# Revit family: VF3_DN15-DN100_AMV(E) 55(56)_RFA_1
name_source: partatom
category: Pipe Accessories
units: mm (PartAtom-declared; Revit-internal decimal feet)

## family parameters
Always vertical = Yes
Cut with Voids When Loaded = No
OmniClass Number = 23.65.55.14.17
OmniClass Title = Adjusting/Controlling Valves for Liquid Services
Part Type = Valve - Breaks Into
Round Connector Dimension = Use Diameter
Shared = No
Work Plane-Based = No

## types (13) — shared parameters
082H3020 = AMV(E) 55(56)_RFA : AMV 55_24V_082H3020
082H3021 = AMV(E) 55(56)_RFA : AMV 55_230V_082H3021
082H3023 = AMV(E) 55(56)_RFA : AMV 56_24V_082H3023
082H3024 = AMV(E) 55(56)_RFA : AMV 56_230V_082H3024
082H3025 = AMV(E) 55(56)_RFA : AME 56_082H3025
Actuator Type = AMV(E) 55(56)_RFA : AME 55_082H3022
Adapter Type = Adapter_AMV(E)_RFA : Adapter_AMV(E) 55(56)_DN65-80_065Z0312
C1 = 8 mm  [stored 0.0262467 ft]
Connection = Flange
Description = Motorized Control Valve
H2 = 95 mm
HB2 = 9 mm  [stored 0.0295276 ft]
HB2__ve = -9 mm
HD = 14 mm  [stored 0.0459318 ft]
HT1 = 43 mm
HT2 = 24 mm
IfcExportAs = IfcValveType
IfcExportType = VF3
K = 65 mm
L2D = 130 mm
L2D_Min = 30 mm
LM = 110 mm
LM1 = 55 mm
LOD 200 = No
LOD 350 = Yes
Manufacturer = Danfoss
Max Medium Temperature = 130 °C
Min Medium Temperature = -10 °C
N = 4
N1 = 13 mm
Nominal Pressure = PN 16
Power = 9 VA
R = 8 mm  [stored 0.0262467 ft]
R4 = 3 mm  [stored 0.00984252 ft]
URL = https://store.danfoss.com
V_SMALL LOD 200 = No
Valve Body Material = Danfoss Grey Iron
Voltage = 24 V
Y1 = 15 mm  [stored 0.0492126 ft]
Z = 22 mm
zero-valued in all types: CAT

## per-type parameters (varying)
- VF3_DN20_Kv6.3_065Z0256: A1=3 mm  [stored 0.00984252 ft]; A1_Flow Pipe=168.00°; A2=47.12°; A3=15.00°; A_Flow Pipe=165.00°; Adapter assembly=2 mm  [stored 0.00656168 ft]; C=3 mm  [stored 0.00984252 ft]; C2_ve=-14 mm; C__ve=-3 mm  [stored -0.00984252 ft]; D=20 mm; DN=20 mm; DN65 to DN100=No; DN65 to DN80=No; D_Connection End=60 mm; D_Flange=105 mm; Depth_Flange=14 mm  [stored 0.0459318 ft]; EXT2=-54 mm  [stored -0.177165 ft]; EXT3=18 mm  [stored 0.0590551 ft]; Extrusion Bottom=55 mm; Extrusion Top=27 mm; Extrusion Top 2=8 mm  [stored 0.0262467 ft]; Flange Bottom Depth=14 mm  [stored 0.0459318 ft]; H1=34 mm; HB1=40 mm; HB1__ve=-40 mm  [stored -0.131234 ft]; HB3=3 mm  [stored 0.00984252 ft]; HE=0 mm  [stored 0 ft]; HE1=57 mm; HH1=87 mm; HH2=70 mm; HR=28 mm; HR1=25 mm; Kvs=6.3 m³/h; L=150 mm; L2=75 mm; L_EXT=85 mm; L_S=48 mm; M=3 mm  [stored 0.00984252 ft]; Model=065Z0256; Model Type=VF3_DN20_Kv6.3; N2=5 mm  [stored 0.0164042 ft]; Offset Flow Pipe_1=6 mm  [stored 0.019685 ft]; Offset Flow Pipe_2=6 mm  [stored 0.019685 ft]; R1=23 mm; R1_1=20 mm; R1_1_1=20 mm; R1_2=13 mm; R1_Revolve=10 mm  [stored 0.0328084 ft]; R2=11 mm  [stored 0.0360892 ft]; R2_Revolve=8 mm  [stored 0.0262467 ft]; R6=29 mm; R6_2=31 mm; R_Flange Bottom=53 mm; R_Flow Pipe=17 mm; R_Top=13 mm; R_Vertical Valve=18 mm  [stored 0.0590551 ft]; R_arc=35 mm; Stroke=10 mm; TH1=97 mm; TL=150 mm; V_DN100=No; V_SMALL=Yes; W=105 mm; W1=18 mm  [stored 0.0590551 ft]; W2=20 mm; W2D=14 mm  [stored 0.0459318 ft]; Weight=3.55 kg; l_Top=3 mm  [stored 0.00984252 ft]
- VF3_DN25_Kv10_065Z0257: A1=5 mm  [stored 0.0164042 ft]; A1_Flow Pipe=166.00°; A2=47.12°; A3=10.00°; A_Flow Pipe=165.00°; Adapter assembly=2 mm  [stored 0.00656168 ft]; C=3 mm  [stored 0.00984252 ft]; C2_ve=-14 mm; C__ve=-3 mm  [stored -0.00984252 ft]; D=25 mm; DN=25 mm; DN65 to DN100=No; DN65 to DN80=No; D_Connection End=70 mm; D_Flange=115 mm; Depth_Flange=14 mm  [stored 0.0459318 ft]; EXT2=-58 mm  [stored -0.190289 ft]; EXT3=15 mm  [stored 0.0492126 ft]; Extrusion Bottom=62 mm; Extrusion Top=25 mm; Extrusion Top 2=5 mm  [stored 0.0164042 ft]; Flange Bottom Depth=15 mm  [stored 0.0492126 ft]; H1=37 mm; HB1=40 mm; HB1__ve=-40 mm  [stored -0.131234 ft]; HB3=3 mm  [stored 0.00984252 ft]; HE=0 mm  [stored 0 ft]; HE1=60 mm; HH1=91 mm; HH2=75 mm; HR=31 mm; HR1=25 mm; Kvs=10.0 m³/h; L=160 mm; L2=80 mm; L_EXT=90 mm; L_S=48 mm; M=3 mm  [stored 0.00984252 ft]; Model=065Z0257; Model Type=VF3_DN25_Kv10; N2=5 mm  [stored 0.0164042 ft]; Offset Flow Pipe_1=9 mm  [stored 0.0295276 ft]; Offset Flow Pipe_2=6 mm  [stored 0.019685 ft]; R1=25 mm; R1_1=21 mm; R1_1_1=21 mm; R1_2=13 mm; R1_Revolve=12 mm  [stored 0.0393701 ft]; R2=11 mm  [stored 0.0360892 ft]; R2_Revolve=9 mm  [stored 0.0295276 ft]; R6=34 mm; R6_2=36 mm; R_Flange Bottom=58 mm; R_Flow Pipe=19 mm  [stored 0.062336 ft]; R_Top=13 mm; R_Vertical Valve=20 mm; R_arc=36 mm; Stroke=10 mm; TH1=101 mm; TL=160 mm; V_DN100=No; V_SMALL=Yes; W=115 mm; W1=18 mm  [stored 0.0590551 ft]; W2=20 mm; W2D=15 mm  [stored 0.0492126 ft]; Weight=4.54 kg; l_Top=3 mm  [stored 0.00984252 ft]
- VF3_DN32_Kv16_065Z0258: A1=3 mm  [stored 0.00984252 ft]; A1_Flow Pipe=170.00°; A2=47.12°; A3=16.00°; A_Flow Pipe=168.00°; Adapter assembly=1 mm  [stored 0.00328084 ft]; C=3 mm  [stored 0.00984252 ft]; C2_ve=-16 mm  [stored -0.0524934 ft]; C__ve=-3 mm  [stored -0.00984252 ft]; D=32 mm; DN=32 mm; DN65 to DN100=No; DN65 to DN80=No; D_Connection End=80 mm; D_Flange=140 mm; Depth_Flange=16 mm  [stored 0.0524934 ft]; EXT2=-62 mm; EXT3=20 mm; Extrusion Bottom=73 mm; Extrusion Top=35 mm; Extrusion Top 2=10 mm  [stored 0.0328084 ft]; Flange Bottom Depth=16 mm  [stored 0.0524934 ft]; H1=42 mm; HB1=40 mm; HB1__ve=-40 mm  [stored -0.131234 ft]; HB3=3 mm  [stored 0.00984252 ft]; HE=0 mm  [stored 0 ft]; HE1=65 mm; HH1=96 mm; HH2=80 mm; HR=31 mm; HR1=33 mm; Kvs=16.0 m³/h; L=180 mm; L2=90 mm; L_EXT=100 mm; L_S=48 mm; M=3 mm  [stored 0.00984252 ft]; Model=065Z0258; Model Type=VF3_DN32_Kv16; N2=5 mm  [stored 0.0164042 ft]; Offset Flow Pipe_1=7 mm  [stored 0.0229659 ft]; Offset Flow Pipe_2=9 mm  [stored 0.0295276 ft]; R1=29 mm; R1_1=24 mm; R1_1_1=24 mm; R1_2=24 mm; R1_Revolve=17 mm; R2=13 mm; R2_Revolve=14 mm  [stored 0.0459318 ft]; R6=39 mm; R6_2=42 mm; R_Flange Bottom=70 mm; R_Flow Pipe=24 mm; R_Top=13 mm; R_Vertical Valve=25 mm; R_arc=41 mm; Stroke=15 mm; TH1=106 mm; TL=180 mm; V_DN100=No; V_SMALL=Yes; W=140 mm; W1=22 mm; W2=26 mm; W2D=15 mm  [stored 0.0492126 ft]; Weight=6.90 kg; l_Top=3 mm  [stored 0.00984252 ft]
- VF3_DN40_Kv25_065Z0259: A1=3 mm  [stored 0.00984252 ft]; A1_Flow Pipe=165.00°; A2=47.12°; A3=15.00°; A_Flow Pipe=166.00°; Adapter assembly=1 mm  [stored 0.00328084 ft]; C=3 mm  [stored 0.00984252 ft]; C2_ve=-16 mm  [stored -0.0524934 ft]; C__ve=-3 mm  [stored -0.00984252 ft]; D=40 mm; DN=40 mm; DN65 to DN100=No; DN65 to DN80=No; D_Connection End=90 mm; D_Flange=150 mm; Depth_Flange=16 mm  [stored 0.0524934 ft]; EXT2=-72 mm; EXT3=30 mm; Extrusion Bottom=74 mm; Extrusion Top=37 mm; Extrusion Top 2=10 mm  [stored 0.0328084 ft]; Flange Bottom Depth=16 mm  [stored 0.0524934 ft]; H1=65 mm; HB1=40 mm; HB1__ve=-40 mm  [stored -0.131234 ft]; HB3=3 mm  [stored 0.00984252 ft]; HE=6 mm  [stored 0.019685 ft]; HE1=94 mm; HH1=124 mm; HH2=90 mm; HR=40 mm; HR1=42 mm; Kvs=25.0 m³/h; L=200 mm; L2=100 mm; L_EXT=120 mm; L_S=48 mm; M=3 mm  [stored 0.00984252 ft]; Model=065Z0259; Model Type=VF3_DN40_Kv25; N2=12 mm  [stored 0.0393701 ft]; Offset Flow Pipe_1=10 mm  [stored 0.0328084 ft]; Offset Flow Pipe_2=10 mm  [stored 0.0328084 ft]; R1=36 mm; R1_1=29 mm; R1_1_1=29 mm; R1_2=18 mm  [stored 0.0590551 ft]; R1_Revolve=25 mm; R2=11 mm  [stored 0.0360892 ft]; R2_Revolve=23 mm; R6=44 mm; R6_2=47 mm; R_Flange Bottom=75 mm; R_Flow Pipe=28 mm; R_Top=13 mm; R_Vertical Valve=29 mm; R_arc=50 mm; Stroke=15 mm; TH1=134 mm; TL=200 mm; V_DN100=No; V_SMALL=Yes; W=150 mm; W1=23 mm; W2=31 mm; W2D=15 mm  [stored 0.0492126 ft]; Weight=9.05 kg; l_Top=3 mm  [stored 0.00984252 ft]
- VF3_DN50_Kv40_065Z0260: A1=1 mm  [stored 0.00328084 ft]; A1_Flow Pipe=165.00°; A2=47.12°; A3=20.00°; A_Flow Pipe=168.00°; Adapter assembly=1 mm  [stored 0.00328084 ft]; C=4 mm  [stored 0.0131234 ft]; C2_ve=-16 mm  [stored -0.0524934 ft]; C__ve=-4 mm  [stored -0.0131234 ft]; D=50 mm; DN=50 mm; DN65 to DN100=No; DN65 to DN80=No; D_Connection End=105 mm; D_Flange=165 mm; Depth_Flange=16 mm  [stored 0.0524934 ft]; EXT2=-80 mm  [stored -0.262467 ft]; EXT3=30 mm; Extrusion Bottom=83 mm; Extrusion Top=50 mm; Extrusion Top 2=10 mm  [stored 0.0328084 ft]; Flange Bottom Depth=16 mm  [stored 0.0524934 ft]; H1=77 mm; HB1=40 mm; HB1__ve=-40 mm  [stored -0.131234 ft]; HB3=4 mm  [stored 0.0131234 ft]; HE=6 mm  [stored 0.019685 ft]; HE1=106 mm; HH1=137 mm; HH2=100 mm; HR=46 mm; HR1=55 mm; Kvs=40.0 m³/h; L=230 mm; L2=115 mm; L_EXT=150 mm; L_S=65 mm; M=3 mm  [stored 0.00984252 ft]; Model=065Z0260; Model Type=VF3_DN50_Kv40; N2=21 mm; Offset Flow Pipe_1=8 mm  [stored 0.0262467 ft]; Offset Flow Pipe_2=15 mm  [stored 0.0492126 ft]; R1=44 mm; R1_1=35 mm; R1_1_1=35 mm; R1_2=21 mm; R1_Revolve=33 mm; R2=11 mm  [stored 0.0360892 ft]; R2_Revolve=28 mm; R6=51 mm; R6_2=54 mm; R_Flange Bottom=83 mm; R_Flow Pipe=30 mm; R_Top=13 mm; R_Vertical Valve=37 mm; R_arc=59 mm; Stroke=15 mm; TH1=147 mm; TL=230 mm; V_DN100=No; V_SMALL=Yes; W=165 mm; W1=32 mm; W2=34 mm; W2D=15 mm  [stored 0.0492126 ft]; Weight=12.79 kg; l_Top=3 mm  [stored 0.00984252 ft]
- VF3_DN65_Kv63_065Z0261: A1=70 mm; A1_Flow Pipe=165.00°; A2=30.00°; A3=20.00°; A_Flow Pipe=165.00°; Adapter assembly=5 mm  [stored 0.0164042 ft]; C=4 mm  [stored 0.0131234 ft]; C2_ve=-18 mm  [stored -0.0590551 ft]; C__ve=-4 mm  [stored -0.0131234 ft]; D=65 mm; DN=65 mm; DN65 to DN100=Yes; DN65 to DN80=Yes; D_Connection End=105 mm; D_Flange=185 mm; Depth_Flange=18 mm  [stored 0.0590551 ft]; EXT2=-97 mm  [stored -0.318241 ft]; EXT3=41 mm; Extrusion Bottom=100 mm; Extrusion Top=65 mm; Extrusion Top 2=20 mm; Flange Bottom Depth=20 mm; H1=84 mm; HB1=45 mm; HB1__ve=-45 mm  [stored -0.147638 ft]; HB3=5 mm  [stored 0.0164042 ft]; HE=7 mm  [stored 0.0229659 ft]; HE1=112 mm; HH1=148 mm; HH2=120 mm; HR=58 mm; HR1=70 mm; Kvs=63.0 m³/h; L=290 mm; L2=145 mm; L_EXT=185 mm; L_S=97 mm; M=3 mm  [stored 0.00984252 ft]; Model=065Z0261; Model Type=VF3_DN65_Kv63; N2=27 mm; Offset Flow Pipe_1=16 mm  [stored 0.0524934 ft]; Offset Flow Pipe_2=25 mm; R1=55 mm; R1_1=50 mm; R1_1_1=50 mm; R1_2=27 mm; R1_Revolve=48 mm; R2=11 mm  [stored 0.0360892 ft]; R2_Revolve=39 mm; R6=61 mm; R6_2=66 mm; R_Flange Bottom=93 mm; R_Flow Pipe=41 mm; R_Top=13 mm; R_Vertical Valve=45 mm; R_arc=76 mm; Stroke=20 mm; TH1=158 mm; TL=290 mm; V_DN100=No; V_SMALL=Yes; W=185 mm; W1=35 mm; W2=48 mm; W2D=15 mm  [stored 0.0492126 ft]; Weight=19.18 kg; l_Top=3 mm  [stored 0.00984252 ft]
- VF3_DN80_Kv100_065Z0262: A1=95 mm; A1_Flow Pipe=165.00°; A2=41.00°; A3=25.00°; A_Flow Pipe=169.00°; Adapter assembly=5 mm  [stored 0.0164042 ft]; C=6 mm  [stored 0.019685 ft]; C2_ve=-19 mm  [stored -0.062336 ft]; C__ve=-6 mm; D=80 mm; DN=80 mm; DN65 to DN100=Yes; DN65 to DN80=Yes; D_Connection End=130 mm; D_Flange=200 mm; Depth_Flange=19 mm  [stored 0.062336 ft]; EXT2=-130 mm  [stored -0.426509 ft]; EXT3=50 mm; Extrusion Bottom=132 mm; Extrusion Top=83 mm; Extrusion Top 2=20 mm; Flange Bottom Depth=20 mm; H1=100 mm; HB1=50 mm; HB1__ve=-50 mm  [stored -0.164042 ft]; HB3=4 mm  [stored 0.0131234 ft]; HE=7 mm  [stored 0.0229659 ft]; HE1=128 mm; HH1=164 mm; HH2=155 mm; HR=68 mm; HR1=70 mm; Kvs=100.0 m³/h; L=316 mm; L2=158 mm; L_EXT=200 mm; L_S=95 mm; M=3 mm  [stored 0.00984252 ft]; Model=065Z0262; Model Type=VF3_DN80_Kv100; N2=25 mm; Offset Flow Pipe_1=25 mm; Offset Flow Pipe_2=21 mm; R1=63 mm; R1_1=56 mm; R1_1_1=55 mm; R1_2=27 mm; R1_Revolve=63 mm; R2=100 mm; R2_Revolve=50 mm; R6=64 mm; R6_2=69 mm; R_Flange Bottom=100 mm; R_Flow Pipe=44 mm; R_Top=13 mm; R_Vertical Valve=55 mm; R_arc=94 mm; Stroke=20 mm; TH1=174 mm; TL=316 mm; V_DN100=No; V_SMALL=Yes; W=200 mm; W1=40 mm; W2=55 mm; W2D=15 mm  [stored 0.0492126 ft]; Weight=23.73 kg; l_Top=3 mm  [stored 0.00984252 ft]
- VF3_DN15_Kv2.5_065Z0254: A1=3 mm  [stored 0.00984252 ft]; A1_Flow Pipe=168.00°; A2=47.12°; A3=13.00°; A_Flow Pipe=166.00°; Adapter assembly=2 mm  [stored 0.00656168 ft]; C=3 mm  [stored 0.00984252 ft]; C2_ve=-12 mm  [stored -0.0393701 ft]; C__ve=-3 mm  [stored -0.00984252 ft]; D=15 mm  [stored 0.0492126 ft]; DN=15 mm; DN65 to DN100=No; DN65 to DN80=No; D_Connection End=50 mm; D_Flange=95 mm; Depth_Flange=12 mm  [stored 0.0393701 ft]; EXT2=-50 mm  [stored -0.164042 ft]; EXT3=20 mm; Extrusion Bottom=49 mm; Extrusion Top=21 mm; Extrusion Top 2=5 mm  [stored 0.0164042 ft]; Flange Bottom Depth=12 mm  [stored 0.0393701 ft]; H1=31 mm; HB1=40 mm; HB1__ve=-40 mm  [stored -0.131234 ft]; HB3=3 mm  [stored 0.00984252 ft]; HE=0 mm  [stored 0 ft]; HE1=54 mm; HH1=85 mm; HH2=63 mm; HR=27 mm; HR1=23 mm; Kvs=2.5 m³/h; L=130 mm; L2=65 mm; L_EXT=80 mm; L_S=48 mm; M=2 mm  [stored 0.00656168 ft]; Model=065Z0254; Model Type=VF3_DN15_Kv2.5; N2=5 mm  [stored 0.0164042 ft]; Offset Flow Pipe_1=7 mm  [stored 0.0229659 ft]; Offset Flow Pipe_2=6 mm  [stored 0.019685 ft]; R1=21 mm; R1_1=16 mm  [stored 0.0524934 ft]; R1_1_1=16 mm  [stored 0.0524934 ft]; R1_2=13 mm; R1_Revolve=9 mm  [stored 0.0295276 ft]; R2=11 mm  [stored 0.0360892 ft]; R2_Revolve=6 mm  [stored 0.019685 ft]; R6=23 mm; R6_2=26 mm; R_Flange Bottom=48 mm; R_Flow Pipe=15 mm  [stored 0.0492126 ft]; R_Top=13 mm; R_Vertical Valve=18 mm  [stored 0.0590551 ft]; R_arc=30 mm; Stroke=10 mm; TH1=95 mm; TL=130 mm; V_DN100=No; V_SMALL=Yes; W=95 mm; W1=17 mm; W2=16 mm  [stored 0.0524934 ft]; W2D=15 mm  [stored 0.0492126 ft]; Weight=2.61 kg; l_Top=3 mm  [stored 0.00984252 ft]
- VF3_DN100_Kv145_065B1685: A1=43 mm; A1_Flow Pipe=165.00°; A2=44.00°; A3=0.00°; A_Flow Pipe=166.00°; Adapter assembly=0 mm  [stored 0 ft]; C=4 mm  [stored 0.0131234 ft]; C2_ve=-19 mm  [stored -0.062336 ft]; C__ve=-4 mm  [stored -0.0131234 ft]; D=100 mm; DN=100 mm; DN65 to DN100=Yes; DN65 to DN80=No; D_Connection End=164 mm; D_Flange=220 mm; Depth_Flange=19 mm  [stored 0.062336 ft]; EXT2=-155 mm  [stored -0.50853 ft]; EXT3=0 mm  [stored 0 ft]; Extrusion Bottom=152 mm; Extrusion Top=67 mm; Extrusion Top 2=20 mm; Flange Bottom Depth=21 mm; H1=78 mm; HB1=50 mm; HB1__ve=-50 mm  [stored -0.164042 ft]; HB3=4 mm  [stored 0.0131234 ft]; HE=0 mm  [stored 0 ft]; HE1=120 mm; HH1=132 mm; HH2=175 mm; HR=49 mm; HR1=75 mm; Kvs=145.0 m³/h; L=350 mm; L2=175 mm; L_EXT=19 mm  [stored 0.062336 ft]; L_S=95 mm; M=3 mm  [stored 0.00984252 ft]; Model=065B1685; Model Type=VF3_DN100_Kv145; N2=25 mm; Offset Flow Pipe_1=25 mm; Offset Flow Pipe_2=33 mm; R1=63 mm; R1_1=59 mm; R1_1_1=35 mm; R1_2=17 mm; R1_Revolve=44 mm; R2=100 mm; R2_Revolve=38 mm; R6=78 mm; R6_2=85 mm; R_Flange Bottom=110 mm; R_Flow Pipe=45 mm; R_Top=18 mm  [stored 0.0590551 ft]; R_Vertical Valve=70 mm; R_arc=94 mm; Stroke=30 mm; TH1=142 mm; TL=350 mm; V_DN100=Yes; V_SMALL=No; W=220 mm; W1=40 mm; W2=35 mm; W2D=15 mm  [stored 0.0492126 ft]; Weight=34.00 kg; l_Top=6 mm  [stored 0.019685 ft]
- VF3_DN15_Kv4.0_065Z0255: A1=3 mm  [stored 0.00984252 ft]; A1_Flow Pipe=168.00°; A2=47.12°; A3=13.00°; A_Flow Pipe=166.00°; Adapter assembly=2 mm  [stored 0.00656168 ft]; C=3 mm  [stored 0.00984252 ft]; C2_ve=-12 mm  [stored -0.0393701 ft]; C__ve=-3 mm  [stored -0.00984252 ft]; D=15 mm  [stored 0.0492126 ft]; DN=15 mm; DN65 to DN100=No; DN65 to DN80=No; D_Connection End=50 mm; D_Flange=95 mm; Depth_Flange=12 mm  [stored 0.0393701 ft]; EXT2=-50 mm  [stored -0.164042 ft]; EXT3=20 mm; Extrusion Bottom=49 mm; Extrusion Top=21 mm; Extrusion Top 2=5 mm  [stored 0.0164042 ft]; Flange Bottom Depth=12 mm  [stored 0.0393701 ft]; H1=31 mm; HB1=40 mm; HB1__ve=-40 mm  [stored -0.131234 ft]; HB3=3 mm  [stored 0.00984252 ft]; HE=0 mm  [stored 0 ft]; HE1=54 mm; HH1=85 mm; HH2=63 mm; HR=27 mm; HR1=23 mm; Kvs=4.0 m³/h; L=130 mm; L2=65 mm; L_EXT=80 mm; L_S=48 mm; M=2 mm  [stored 0.00656168 ft]; Model=065Z0255; Model Type=VF3_DN15_Kv4.0; N2=5 mm  [stored 0.0164042 ft]; Offset Flow Pipe_1=7 mm  [stored 0.0229659 ft]; Offset Flow Pipe_2=6 mm  [stored 0.019685 ft]; R1=21 mm; R1_1=16 mm  [stored 0.0524934 ft]; R1_1_1=16 mm  [stored 0.0524934 ft]; R1_2=13 mm; R1_Revolve=9 mm  [stored 0.0295276 ft]; R2=11 mm  [stored 0.0360892 ft]; R2_Revolve=6 mm  [stored 0.019685 ft]; R6=23 mm; R6_2=26 mm; R_Flange Bottom=48 mm; R_Flow Pipe=15 mm  [stored 0.0492126 ft]; R_Top=13 mm; R_Vertical Valve=18 mm  [stored 0.0590551 ft]; R_arc=30 mm; Stroke=10 mm; TH1=95 mm; TL=130 mm; V_DN100=No; V_SMALL=Yes; W=95 mm; W1=17 mm; W2=16 mm  [stored 0.0524934 ft]; W2D=15 mm  [stored 0.0492126 ft]; Weight=2.61 kg; l_Top=3 mm  [stored 0.00984252 ft]
- VF3_DN15_Kv1.6_065Z0253: A1=3 mm  [stored 0.00984252 ft]; A1_Flow Pipe=168.00°; A2=47.12°; A3=13.00°; A_Flow Pipe=166.00°; Adapter assembly=2 mm  [stored 0.00656168 ft]; C=3 mm  [stored 0.00984252 ft]; C2_ve=-12 mm  [stored -0.0393701 ft]; C__ve=-3 mm  [stored -0.00984252 ft]; D=15 mm  [stored 0.0492126 ft]; DN=15 mm; DN65 to DN100=No; DN65 to DN80=No; D_Connection End=50 mm; D_Flange=95 mm; Depth_Flange=12 mm  [stored 0.0393701 ft]; EXT2=-50 mm  [stored -0.164042 ft]; EXT3=20 mm; Extrusion Bottom=49 mm; Extrusion Top=21 mm; Extrusion Top 2=5 mm  [stored 0.0164042 ft]; Flange Bottom Depth=12 mm  [stored 0.0393701 ft]; H1=31 mm; HB1=40 mm; HB1__ve=-40 mm  [stored -0.131234 ft]; HB3=3 mm  [stored 0.00984252 ft]; HE=0 mm  [stored 0 ft]; HE1=54 mm; HH1=85 mm; HH2=63 mm; HR=27 mm; HR1=23 mm; Kvs=1.6 m³/h; L=130 mm; L2=65 mm; L_EXT=80 mm; L_S=48 mm; M=2 mm  [stored 0.00656168 ft]; Model=065Z0253; Model Type=VF3_DN15_Kv1.6; N2=5 mm  [stored 0.0164042 ft]; Offset Flow Pipe_1=7 mm  [stored 0.0229659 ft]; Offset Flow Pipe_2=6 mm  [stored 0.019685 ft]; R1=21 mm; R1_1=16 mm  [stored 0.0524934 ft]; R1_1_1=16 mm  [stored 0.0524934 ft]; R1_2=13 mm; R1_Revolve=9 mm  [stored 0.0295276 ft]; R2=11 mm  [stored 0.0360892 ft]; R2_Revolve=6 mm  [stored 0.019685 ft]; R6=23 mm; R6_2=26 mm; R_Flange Bottom=48 mm; R_Flow Pipe=15 mm  [stored 0.0492126 ft]; R_Top=13 mm; R_Vertical Valve=18 mm  [stored 0.0590551 ft]; R_arc=30 mm; Stroke=10 mm; TH1=95 mm; TL=130 mm; V_DN100=No; V_SMALL=Yes; W=95 mm; W1=17 mm; W2=16 mm  [stored 0.0524934 ft]; W2D=15 mm  [stored 0.0492126 ft]; Weight=2.61 kg; l_Top=3 mm  [stored 0.00984252 ft]
- VF3_DN15_Kv1.0_065Z0252: A1=3 mm  [stored 0.00984252 ft]; A1_Flow Pipe=168.00°; A2=47.12°; A3=13.00°; A_Flow Pipe=166.00°; Adapter assembly=2 mm  [stored 0.00656168 ft]; C=3 mm  [stored 0.00984252 ft]; C2_ve=-12 mm  [stored -0.0393701 ft]; C__ve=-3 mm  [stored -0.00984252 ft]; D=15 mm  [stored 0.0492126 ft]; DN=15 mm; DN65 to DN100=No; DN65 to DN80=No; D_Connection End=50 mm; D_Flange=95 mm; Depth_Flange=12 mm  [stored 0.0393701 ft]; EXT2=-50 mm  [stored -0.164042 ft]; EXT3=20 mm; Extrusion Bottom=49 mm; Extrusion Top=21 mm; Extrusion Top 2=5 mm  [stored 0.0164042 ft]; Flange Bottom Depth=12 mm  [stored 0.0393701 ft]; H1=31 mm; HB1=40 mm; HB1__ve=-40 mm  [stored -0.131234 ft]; HB3=3 mm  [stored 0.00984252 ft]; HE=0 mm  [stored 0 ft]; HE1=54 mm; HH1=85 mm; HH2=63 mm; HR=27 mm; HR1=23 mm; Kvs=1.0 m³/h; L=130 mm; L2=65 mm; L_EXT=80 mm; L_S=48 mm; M=2 mm  [stored 0.00656168 ft]; Model=065Z0252; Model Type=VF3_DN15_Kv1.0; N2=5 mm  [stored 0.0164042 ft]; Offset Flow Pipe_1=7 mm  [stored 0.0229659 ft]; Offset Flow Pipe_2=6 mm  [stored 0.019685 ft]; R1=21 mm; R1_1=16 mm  [stored 0.0524934 ft]; R1_1_1=16 mm  [stored 0.0524934 ft]; R1_2=13 mm; R1_Revolve=9 mm  [stored 0.0295276 ft]; R2=11 mm  [stored 0.0360892 ft]; R2_Revolve=6 mm  [stored 0.019685 ft]; R6=23 mm; R6_2=26 mm; R_Flange Bottom=48 mm; R_Flow Pipe=15 mm  [stored 0.0492126 ft]; R_Top=13 mm; R_Vertical Valve=18 mm  [stored 0.0590551 ft]; R_arc=30 mm; Stroke=10 mm; TH1=95 mm; TL=130 mm; V_DN100=No; V_SMALL=Yes; W=95 mm; W1=17 mm; W2=16 mm  [stored 0.0524934 ft]; W2D=15 mm  [stored 0.0492126 ft]; Weight=2.61 kg; l_Top=3 mm  [stored 0.00984252 ft]
- VF3_DN15_Kv0.63_065Z0251: A1=3 mm  [stored 0.00984252 ft]; A1_Flow Pipe=168.00°; A2=47.12°; A3=13.00°; A_Flow Pipe=166.00°; Adapter assembly=2 mm  [stored 0.00656168 ft]; C=3 mm  [stored 0.00984252 ft]; C2_ve=-12 mm  [stored -0.0393701 ft]; C__ve=-3 mm  [stored -0.00984252 ft]; D=15 mm  [stored 0.0492126 ft]; DN=15 mm; DN65 to DN100=No; DN65 to DN80=No; D_Connection End=50 mm; D_Flange=95 mm; Depth_Flange=12 mm  [stored 0.0393701 ft]; EXT2=-50 mm  [stored -0.164042 ft]; EXT3=20 mm; Extrusion Bottom=49 mm; Extrusion Top=21 mm; Extrusion Top 2=5 mm  [stored 0.0164042 ft]; Flange Bottom Depth=12 mm  [stored 0.0393701 ft]; H1=31 mm; HB1=40 mm; HB1__ve=-40 mm  [stored -0.131234 ft]; HB3=3 mm  [stored 0.00984252 ft]; HE=0 mm  [stored 0 ft]; HE1=54 mm; HH1=85 mm; HH2=63 mm; HR=27 mm; HR1=23 mm; Kvs=0.6 m³/h; L=130 mm; L2=65 mm; L_EXT=80 mm; L_S=48 mm; M=2 mm  [stored 0.00656168 ft]; Model=065Z0251; Model Type=VF3_DN15_Kv0.63; N2=5 mm  [stored 0.0164042 ft]; Offset Flow Pipe_1=7 mm  [stored 0.0229659 ft]; Offset Flow Pipe_2=6 mm  [stored 0.019685 ft]; R1=21 mm; R1_1=16 mm  [stored 0.0524934 ft]; R1_1_1=16 mm  [stored 0.0524934 ft]; R1_2=13 mm; R1_Revolve=9 mm  [stored 0.0295276 ft]; R2=11 mm  [stored 0.0360892 ft]; R2_Revolve=6 mm  [stored 0.019685 ft]; R6=23 mm; R6_2=26 mm; R_Flange Bottom=48 mm; R_Flow Pipe=15 mm  [stored 0.0492126 ft]; R_Top=13 mm; R_Vertical Valve=18 mm  [stored 0.0590551 ft]; R_arc=30 mm; Stroke=10 mm; TH1=95 mm; TL=130 mm; V_DN100=No; V_SMALL=Yes; W=95 mm; W1=17 mm; W2=16 mm  [stored 0.0524934 ft]; W2D=15 mm  [stored 0.0492126 ft]; Weight=2.61 kg; l_Top=3 mm  [stored 0.00984252 ft]

note: [stored X ft] marks values corroborated as IEEE doubles in the binary element streams (Revit-internal decimal feet)

## geometry (parser evidence)
native form markers: Revolve x2, Sweep x7
no freeform markers — native parametric forms only
